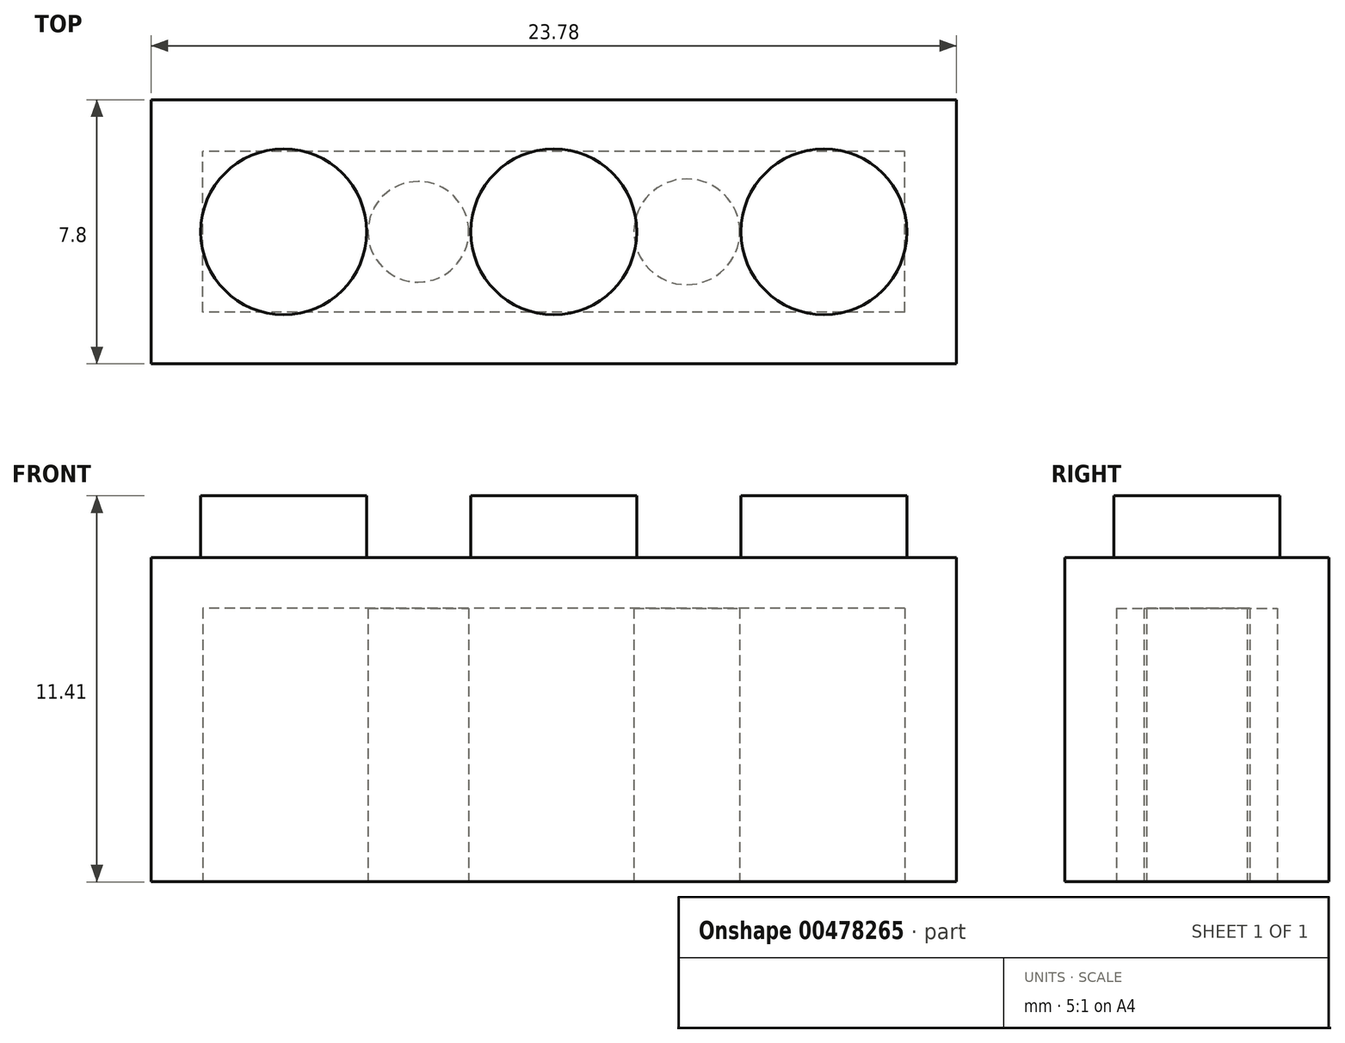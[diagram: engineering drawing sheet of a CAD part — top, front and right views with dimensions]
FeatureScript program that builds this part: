
annotation { "Feature Type Name" : "Feature", "Feature Type Description" : "" }
export const myFeature = defineFeature(function(context is Context, id is Id, definition is map)
    precondition{}
    {
        {
            var Q0;
            Q0=qCreatedBy(makeId("Top.planeOp"),FACE);
            var sketch = newSketch(context, id + "F0", { "sketchPlane" : qUnion([Q0])});
            skLineSegment(sketch, "E0.bottom", {"start": v(11.89, 3.9) * mm, "end": v(-11.89, 3.9) * mm});
            skLineSegment(sketch, "E0.top", {"start": v(11.89, -3.9) * mm, "end": v(-11.89, -3.9) * mm});
            skLineSegment(sketch, "E0.left", {"start": v(11.89, 3.9) * mm, "end": v(11.89, -3.9) * mm});
            skLineSegment(sketch, "E0.right", {"start": v(-11.89, 3.9) * mm, "end": v(-11.89, -3.9) * mm});
            skPoint(sketch, "E0.middle", {"position": v(0, 0) * mm});
            skSolve(sketch);
        }
        {
            var Q0;
            Q0=makeQuery(id+"F0.imprint","IMPRINT",FACE,{"disambiguationData":[TD([[makeQuery(id+"F0.imprint","IMPRINT",EDGE,{"derivedFrom":sQuery(id+"F0.wireOp",EDGE,"E0.bottom")}),1.0]])]});
            extrude(context, id + "F1", {"entities" : qUnion([Q0]), "endBound" : BoundingType.SYMMETRIC, "depth" : 9.58 * mm, "offsetDistance" : 25.4 * mm});
        }
        {
            var Q0;
            Q0=makeQuery(id+"F1.opExtrude","CAP_FACE",FACE,{"disambiguationData":[OSD([sQuery(id+"F0.wireOp",EDGE,"E0.bottom"),sQuery(id+"F0.wireOp",EDGE,"E0.top"),sQuery(id+"F0.wireOp",EDGE,"E0.left"),sQuery(id+"F0.wireOp",EDGE,"E0.right")])],"isStart":false});
            var sketch = newSketch(context, id + "F2", { "sketchPlane" : qUnion([Q0])});
            skCircle(sketch, "E1", {"center": v(-7.98, 0) * mm, "radius": 2.45 * mm});
            skCircle(sketch, "E2", {"center": v(0, 0) * mm, "radius": 2.45 * mm});
            skCircle(sketch, "E3", {"center": v(7.98, 0) * mm, "radius": 2.45 * mm});
            skSolve(sketch);
        }
        {
            var Q0;
            Q0 = qSketchRegion(id + "F2", true);
            extrude(context, id + "F3", {"entities" : qUnion([Q0]), "operationType" : NewBodyOperationType.ADD, "depth" : 1.83 * mm, "offsetDistance" : 25.4 * mm});
        }
        {
            var Q0;
            Q0=makeQuery(id+"F1.opExtrude","CAP_FACE",FACE,{"disambiguationData":[OSD([sQuery(id+"F0.wireOp",EDGE,"E0.bottom"),sQuery(id+"F0.wireOp",EDGE,"E0.top"),sQuery(id+"F0.wireOp",EDGE,"E0.left"),sQuery(id+"F0.wireOp",EDGE,"E0.right")])],"isStart":true});
            var sketch = newSketch(context, id + "F4", { "sketchPlane" : qUnion([Q0])});
            skLineSegment(sketch, "E4.bottom", {"start": v(10.36, 2.37) * mm, "end": v(-10.36, 2.37) * mm});
            skLineSegment(sketch, "E4.top", {"start": v(10.36, -2.37) * mm, "end": v(-10.36, -2.37) * mm});
            skLineSegment(sketch, "E4.left", {"start": v(10.36, 2.37) * mm, "end": v(10.36, -2.37) * mm});
            skLineSegment(sketch, "E4.right", {"start": v(-10.36, 2.37) * mm, "end": v(-10.36, -2.37) * mm});
            skPoint(sketch, "E4.middle", {"position": v(0, 0) * mm});
            skSolve(sketch);
        }
        {
            var Q0;
            Q0=makeQuery(id+"F4.imprint","IMPRINT",FACE,{"disambiguationData":[TD([[makeQuery(id+"F4.imprint","IMPRINT",EDGE,{"derivedFrom":sQuery(id+"F4.wireOp",EDGE,"E4.bottom")}),1.0]])]});
            var sketch = newSketch(context, id + "F5", { "sketchPlane" : qUnion([Q0])});
            skCircle(sketch, "E5", {"center": v(-4, 0) * mm, "radius": 1.49 * mm});
            skCircle(sketch, "E6", {"center": v(3.92, 0) * mm, "radius": 1.56 * mm});
            skSolve(sketch);
        }
        {
            var Q0;
            Q0=makeQuery(id+"F4.imprint","IMPRINT",FACE,{"disambiguationData":[TD([[makeQuery(id+"F4.imprint","IMPRINT",EDGE,{"derivedFrom":sQuery(id+"F4.wireOp",EDGE,"E4.bottom")}),1.0]])]});
            extrude(context, id + "F6", {"entities" : qUnion([Q0]), "operationType" : NewBodyOperationType.REMOVE, "oppositeDirection" : true, "depth" : 8.08 * mm, "offsetDistance" : 25.4 * mm});
        }
        {
            var Q0;
            Q0=makeQuery(id+"F5.imprint","IMPRINT",FACE,{"disambiguationData":[TD([[makeQuery(id+"F5.imprint","IMPRINT",EDGE,{"derivedFrom":sQuery(id+"F5.wireOp",EDGE,"E5")}),1.0]])]});
            var Q1;
            Q1=makeQuery(id+"F5.imprint","IMPRINT",FACE,{"disambiguationData":[TD([[makeQuery(id+"F5.imprint","IMPRINT",EDGE,{"derivedFrom":sQuery(id+"F5.wireOp",EDGE,"E6")}),1.0]])]});
            extrude(context, id + "F7", {"entities" : qUnion([Q0, Q1]), "operationType" : NewBodyOperationType.ADD, "depth" : -8.08 * mm, "offsetDistance" : 25.4 * mm});
        }
    });
